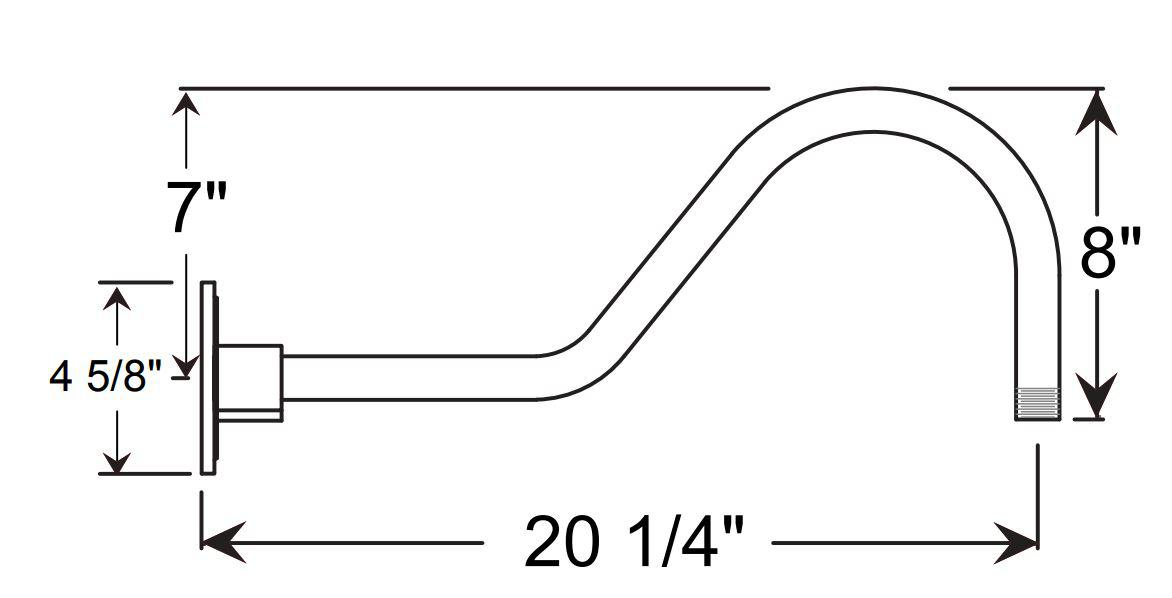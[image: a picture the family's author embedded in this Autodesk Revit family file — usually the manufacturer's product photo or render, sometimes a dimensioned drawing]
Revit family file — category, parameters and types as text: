
# Revit family: Warehouse Deep 20,24,27,30,36,42 MB
name_source: partatom
category: Lighting Fixtures
units: mm (PartAtom-declared; Revit-internal decimal feet)

## family parameters
Always vertical = Yes
Cut with Voids When Loaded = No
Light Source = Yes
OmniClass Number = 23.80.70.00
OmniClass Title = Lighting
Part Type = Normal
Room Calculation Point = No
Round Connector Dimension = Use Diameter
Shared = No
Work Plane-Based = No

## types (6) — shared parameters
Apparent Load = 200 VA
Body Colour = Spun aluminium
Body Material = body
CRI = >90
Color Filter = 16777215
Construction Material = Heavy Duty spun aluminum.
Default Elevation = 0' - 0"
Description = 120-277 Voltage
Dimming = 1%
Dimming Lamp Color Temperature Shift = <None>
Efficiency = 65-125 lumens per watt
Lamp = MB
Life = L70 50,000 hours
Load Classification = Lighting
Manufacturer = ANP Lighting
Photometric Web File = generic
Power Factor = 1
Tilt Angle = 90.00°
URL = https://www.anplighting.com
Voltage = 277 V
Warranty = 5 year limited warranty
Wattage Comments = 200 W Max

## per-type parameters (varying)
| type | BULB | Bulb | Fixture Diameter | Fixture Height | OSWD524 | OSWD527 | OSWD530 | OSWD536 | OSWD542 | WD520 | Weight | a | b |
| OSWD524 | Yes | Bulb | 2' - 0" | 1' - 1" | Yes | No | No | No | No | No | 8.0 lbs | 1' - 1" | 0' - 1" |
| OSWD527 | Yes | Bulb | 2' - 3" | 1' - 3" | No | Yes | No | No | No | No | 6.5lbs | 1' - 3" | 0' - 2" |
| OSWD530 | Yes | Bulb | 2' - 6" | 1' - 3" | No | No | Yes | No | No | No | 13.0 lbs | 1' - 3" | 0' - 2" |
| OSWD536 | Yes | Bulb | 3' - 0" | 1' - 6" | No | No | No | Yes | No | No | 16.5lb | 1' - 6" | 0' - 4" |
| OSWD542 | Yes | Bulb | 3' - 6" | 1' - 9" | No | No | No | No | Yes | No | 21 lbs | 1' - 9" | 0' - 6" |
| WD520 | No | <By Category> | 1' - 9" | 1' - 1 1/2" | No | No | No | No | No | Yes | 3.0 lb | 1' - 1 1/2" | 0' - 2" |

note: column(s) folded — value = type name in every type: Model

## geometry (parser evidence)
native form markers: Sweep x59
no freeform markers — native parametric forms only
